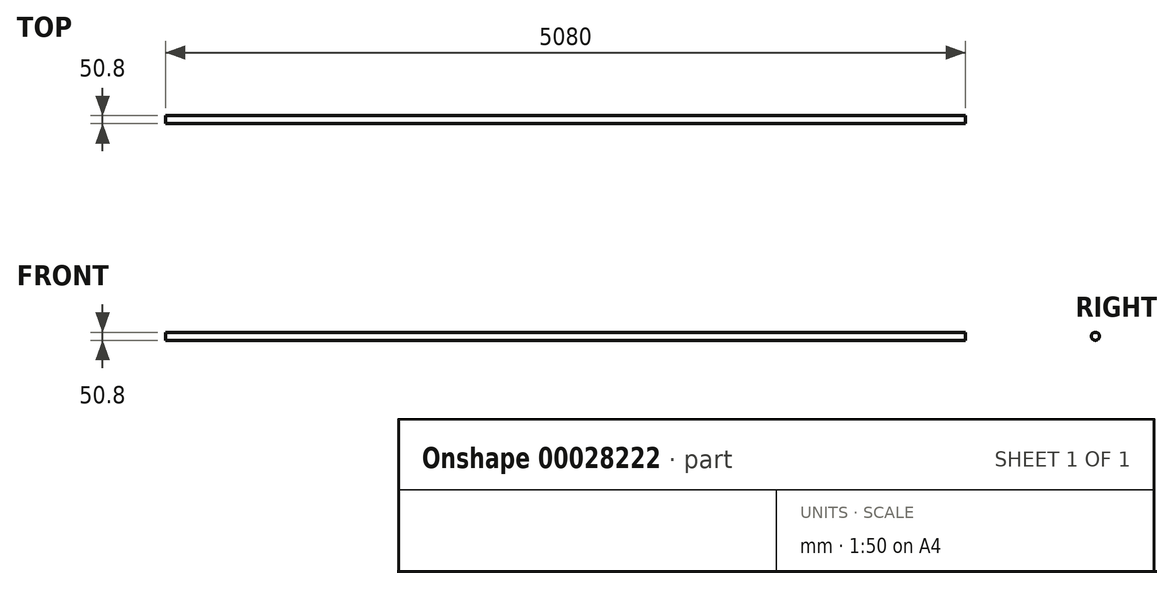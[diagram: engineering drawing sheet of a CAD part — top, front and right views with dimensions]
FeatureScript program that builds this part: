
annotation { "Feature Type Name" : "Feature", "Feature Type Description" : "" }
export const myFeature = defineFeature(function(context is Context, id is Id, definition is map)
    precondition{}
    {
        {
            var Q0;
            Q0=qCreatedBy(makeId("Right.planeOp"),FACE);
            var sketch = newSketch(context, id + "F0", { "sketchPlane" : qUnion([Q0])});
            skCircle(sketch, "E0", {"center": v(-20.12, 20.22) * mm, "radius": 25.4 * mm});
            skSolve(sketch);
        }
        {
            var Q0;
            Q0=makeQuery(id+"F0.imprint","IMPRINT",FACE,{"disambiguationData":[TD([[makeQuery(id+"F0.imprint","IMPRINT",EDGE,{"derivedFrom":sQuery(id+"F0.wireOp",EDGE,"E0")}),1.0]])]});
            extrude(context, id + "F1", {"entities" : qUnion([Q0]), "depth" : 5080 * mm});
        }
    });
